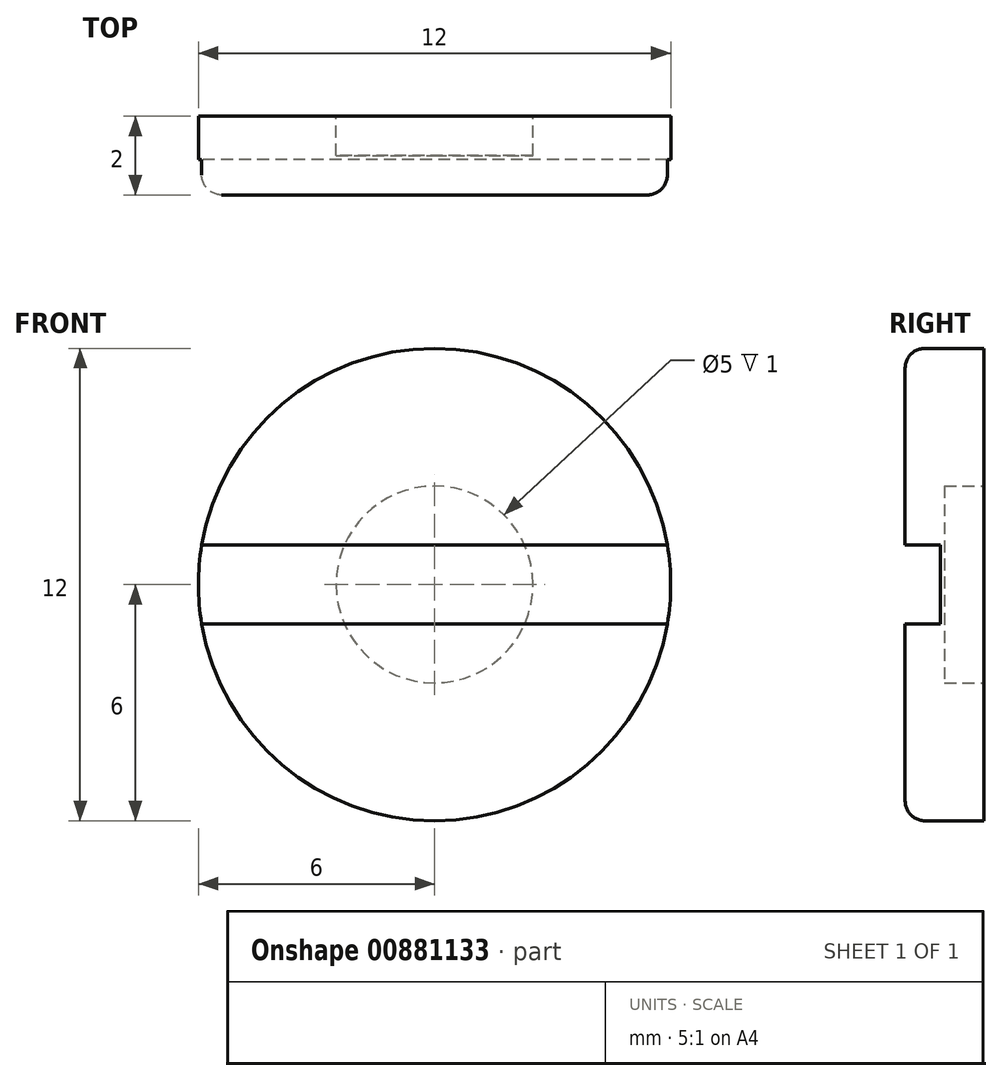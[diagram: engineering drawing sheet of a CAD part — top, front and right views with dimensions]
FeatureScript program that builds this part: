
annotation { "Feature Type Name" : "Feature", "Feature Type Description" : "" }
export const myFeature = defineFeature(function(context is Context, id is Id, definition is map)
    precondition{}
    {
        {
            var Q0;
            Q0=qCreatedBy(makeId("Front.planeOp"),FACE);
            var sketch = newSketch(context, id + "F0", { "sketchPlane" : qUnion([Q0])});
            skCircle(sketch, "E0", {"center": v(0, 0) * mm, "radius": 6 * mm});
            skSolve(sketch);
        }
        {
            var Q0;
            Q0=makeQuery(id+"F0.imprint","IMPRINT",FACE,{"disambiguationData":[TD([[makeQuery(id+"F0.imprint","IMPRINT",EDGE,{"derivedFrom":sQuery(id+"F0.wireOp",EDGE,"E0")}),1.0]])]});
            extrude(context, id + "F1", {"entities" : qUnion([Q0]), "depth" : 2 * mm, "offsetDistance" : 25 * mm});
        }
        {
            var Q0;
            Q0=makeQuery(id+"F1.opExtrude","CAP_FACE",FACE,{"disambiguationData":[OSD([sQuery(id+"F0.wireOp",EDGE,"E0")])],"isStart":true});
            var sketch = newSketch(context, id + "F2", { "sketchPlane" : qUnion([Q0])});
            skCircle(sketch, "E1", {"center": v(0, 0) * mm, "radius": 2.5 * mm});
            skSolve(sketch);
        }
        {
            var Q0;
            Q0=makeQuery(id+"F2.imprint","IMPRINT",FACE,{"disambiguationData":[TD([[makeQuery(id+"F2.imprint","IMPRINT",EDGE,{"derivedFrom":sQuery(id+"F2.wireOp",EDGE,"E1")}),1.0]])]});
            extrude(context, id + "F3", {"entities" : qUnion([Q0]), "operationType" : NewBodyOperationType.REMOVE, "oppositeDirection" : true, "depth" : 1 * mm, "offsetDistance" : 25 * mm});
        }
        {
            var Q0;
            Q0=qCreatedBy(makeId("Right.planeOp"),FACE);
            var sketch = newSketch(context, id + "F4", { "sketchPlane" : qUnion([Q0])});
            skLineSegment(sketch, "E2.bottom", {"start": v(-1.1, 1) * mm, "end": v(-3.1, 1) * mm});
            skLineSegment(sketch, "E2.top", {"start": v(-1.1, -1) * mm, "end": v(-3.1, -1) * mm});
            skLineSegment(sketch, "E2.left", {"start": v(-1.1, 1) * mm, "end": v(-1.1, -1) * mm});
            skLineSegment(sketch, "E2.right", {"start": v(-3.1, 1) * mm, "end": v(-3.1, -1) * mm});
            skSolve(sketch);
        }
        {
            var Q0;
            Q0=makeQuery(id+"F4.imprint","IMPRINT",FACE,{"disambiguationData":[TD([[makeQuery(id+"F4.imprint","IMPRINT",EDGE,{"derivedFrom":sQuery(id+"F4.wireOp",EDGE,"E2.bottom")}),1.0]])]});
            extrude(context, id + "F5", {"entities" : qUnion([Q0]), "operationType" : NewBodyOperationType.REMOVE, "depth" : 25 * mm, "offsetDistance" : 25 * mm, "symmetric" : true});
        }
        {
            var Q0;
            {var subQ0=sQuery(id+"F0.wireOp",EDGE,"E0");Q0=makeQuery(id+"F5.boolean.opBoolean","SPLIT",EDGE,{"disambiguationData":[TD([makeQuery(id+"F5.opExtrude","SWEPT_FACE",FACE,{"disambiguationData":[OSD([sQuery(id+"F4.wireOp",EDGE,"E2.top")])]})])],"derivedFrom":makeQuery(id+"F1.opExtrude","CAP_EDGE",EDGE,{"disambiguationData":[OSD([subQ0])],"isStart":false})});}
            var Q1;
            {var subQ0=sQuery(id+"F0.wireOp",EDGE,"E0");Q1=makeQuery(id+"F5.boolean.opBoolean","SPLIT",EDGE,{"disambiguationData":[TD([makeQuery(id+"F5.opExtrude","SWEPT_FACE",FACE,{"disambiguationData":[OSD([sQuery(id+"F4.wireOp",EDGE,"E2.bottom")])]})])],"derivedFrom":makeQuery(id+"F1.opExtrude","CAP_EDGE",EDGE,{"disambiguationData":[OSD([subQ0])],"isStart":false})});}
            fillet(context, id + "F6", {"entities" : qUnion([Q0, Q1]), "radius" : 0.5 * mm, "tangentPropagation" : true, "allowEdgeOverflow" : false});
        }
    });
